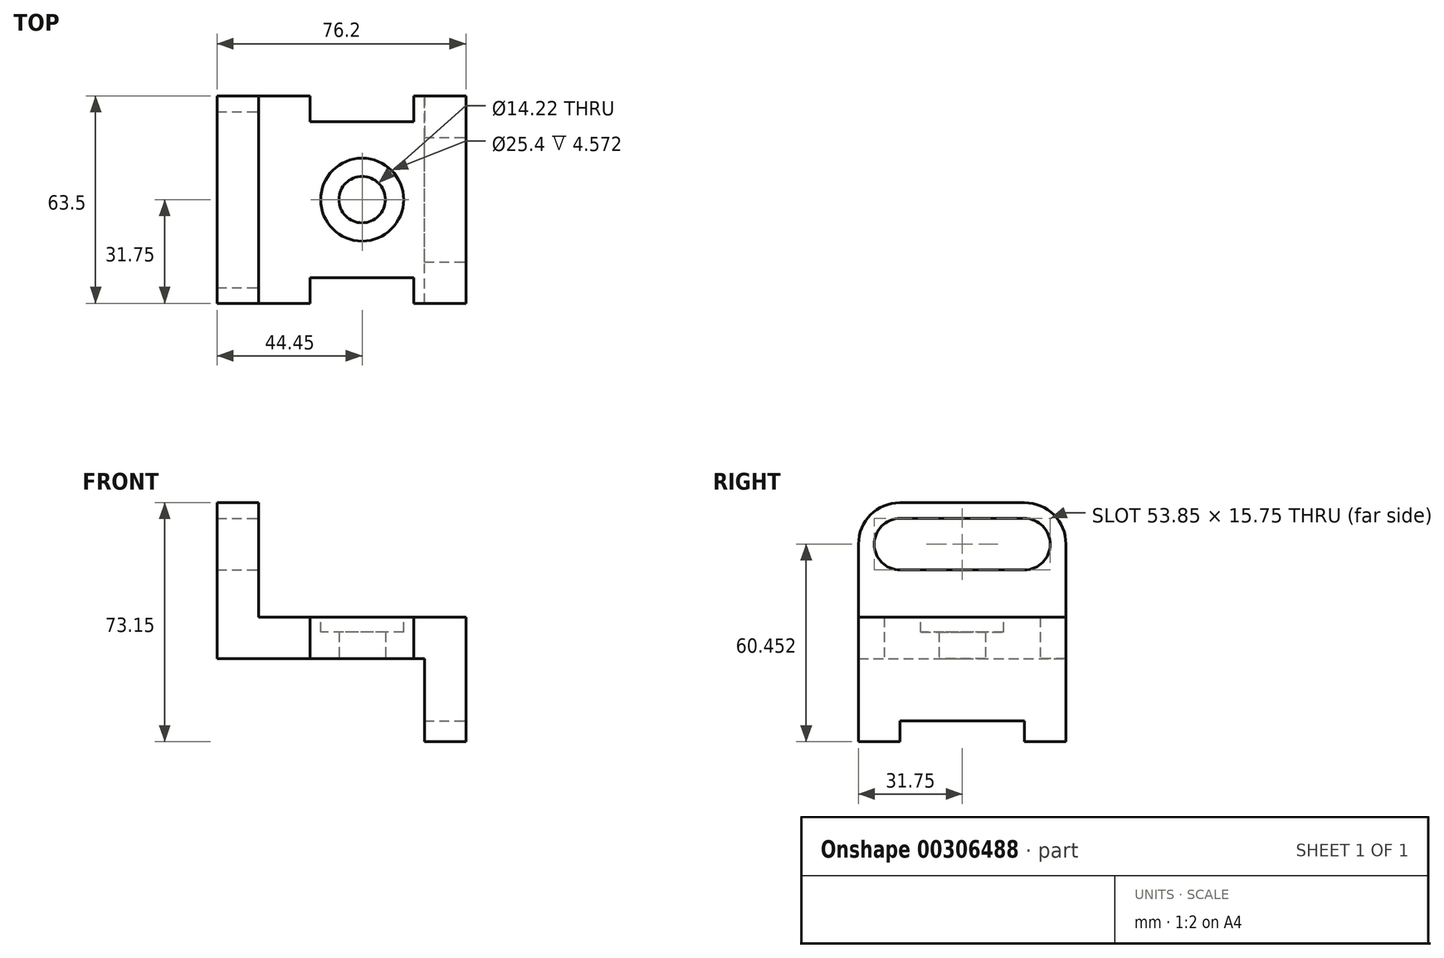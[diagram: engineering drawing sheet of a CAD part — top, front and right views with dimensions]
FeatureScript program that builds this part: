
annotation { "Feature Type Name" : "Feature", "Feature Type Description" : "" }
export const myFeature = defineFeature(function(context is Context, id is Id, definition is map)
    precondition{}
    {
        {
            var Q0;
            Q0=qCreatedBy(makeId("Top.planeOp"),FACE);
            var sketch = newSketch(context, id + "F0", { "sketchPlane" : qUnion([Q0])});
            skLineSegment(sketch, "E0.bottom", {"start": v(0, 0) * mm, "end": v(15.75, 0) * mm});
            skLineSegment(sketch, "E0.top", {"start": v(0, 63.5) * mm, "end": v(15.75, 63.5) * mm});
            skLineSegment(sketch, "E0.left", {"start": v(0, 0) * mm, "end": v(0, 63.5) * mm});
            skLineSegment(sketch, "E0.right", {"start": v(63.5, 0) * mm, "end": v(63.5, 63.5) * mm});
            skLineSegment(sketch, "E1.top", {"start": v(15.75, 7.87) * mm, "end": v(47.5, 7.87) * mm});
            skLineSegment(sketch, "E1.left", {"start": v(15.75, 0) * mm, "end": v(15.75, 7.87) * mm});
            skLineSegment(sketch, "E1.right", {"start": v(47.5, 0) * mm, "end": v(47.5, 7.87) * mm});
            skLineSegment(sketch, "E2.top", {"start": v(15.75, 55.63) * mm, "end": v(47.5, 55.63) * mm});
            skLineSegment(sketch, "E2.left", {"start": v(15.75, 63.5) * mm, "end": v(15.75, 55.63) * mm});
            skLineSegment(sketch, "E2.right", {"start": v(47.5, 63.5) * mm, "end": v(47.5, 55.63) * mm});
            skLineSegment(sketch, "E3.trimOffspring", {"start": v(47.5, 63.5) * mm, "end": v(63.5, 63.5) * mm});
            skLineSegment(sketch, "E4.trimOffspring", {"start": v(47.5, 0) * mm, "end": v(63.5, 0) * mm});
            skCircle(sketch, "E5", {"center": v(31.75, 31.75) * mm, "radius": 7.11 * mm});
            skSolve(sketch);
        }
        {
            var Q0;
            Q0 = qSketchRegion(id + "F0", true);
            extrude(context, id + "F1", {"entities" : qUnion([Q0]), "depth" : 12.7 * mm});
        }
        {
            var Q0;
            Q0=makeQuery(id+"F1.opExtrude","SWEPT_FACE",FACE,{"disambiguationData":[OSD([sQuery(id+"F0.wireOp",EDGE,"E0.right")])]});
            var sketch = newSketch(context, id + "F2", { "sketchPlane" : qUnion([Q0])});
            skLineSegment(sketch, "E6.top", {"start": v(0, -25.4) * mm, "end": v(12.7, -25.4) * mm});
            skLineSegment(sketch, "E6.left", {"start": v(0, -19.05) * mm, "end": v(0, -25.4) * mm});
            skLineSegment(sketch, "E6.right", {"start": v(12.7, -19.05) * mm, "end": v(12.7, -25.4) * mm});
            skLineSegment(sketch, "E7.top", {"start": v(63.5, -25.4) * mm, "end": v(50.8, -25.4) * mm});
            skLineSegment(sketch, "E7.left", {"start": v(63.5, -19.05) * mm, "end": v(63.5, -25.4) * mm});
            skLineSegment(sketch, "E7.right", {"start": v(50.8, -19.05) * mm, "end": v(50.8, -25.4) * mm});
            skLineSegment(sketch, "E8.bottom", {"start": v(12.7, -19.05) * mm, "end": v(50.8, -19.05) * mm});
            skLineSegment(sketch, "E8.top", {"start": v(0, 0) * mm, "end": v(63.5, 0) * mm});
            skLineSegment(sketch, "E8.left", {"start": v(0, -19.05) * mm, "end": v(0, 0) * mm});
            skLineSegment(sketch, "E8.right", {"start": v(63.5, -19.05) * mm, "end": v(63.5, 0) * mm});
            skSolve(sketch);
        }
        {
            var Q0;
            Q0 = qSketchRegion(id + "F2", true);
            extrude(context, id + "F3", {"entities" : qUnion([Q0]), "operationType" : NewBodyOperationType.ADD, "oppositeDirection" : true, "depth" : 12.7 * mm});
        }
        {
            var Q0;
            Q0=makeQuery(id+"F1.opExtrude","CAP_FACE",FACE,{"disambiguationData":[OSD([sQuery(id+"F0.wireOp",EDGE,"E0.bottom"),sQuery(id+"F0.wireOp",EDGE,"E0.top"),sQuery(id+"F0.wireOp",EDGE,"E0.left"),sQuery(id+"F0.wireOp",EDGE,"E0.right"),sQuery(id+"F0.wireOp",EDGE,"E1.top"),sQuery(id+"F0.wireOp",EDGE,"E1.left"),sQuery(id+"F0.wireOp",EDGE,"E1.right"),sQuery(id+"F0.wireOp",EDGE,"E2.top"),sQuery(id+"F0.wireOp",EDGE,"E2.left"),sQuery(id+"F0.wireOp",EDGE,"E2.right"),sQuery(id+"F0.wireOp",EDGE,"E3.trimOffspring"),sQuery(id+"F0.wireOp",EDGE,"E4.trimOffspring"),sQuery(id+"F0.wireOp",EDGE,"E5")])],"isStart":false});
            var sketch = newSketch(context, id + "F4", { "sketchPlane" : qUnion([Q0])});
            skCircle(sketch, "E9", {"center": v(31.75, 31.75) * mm, "radius": 12.7 * mm});
            skSolve(sketch);
        }
        {
            var Q0;
            Q0 = qSketchRegion(id + "F4", true);
            extrude(context, id + "F5", {"entities" : qUnion([Q0]), "operationType" : NewBodyOperationType.REMOVE, "oppositeDirection" : true, "depth" : 4.57 * mm});
        }
        {
            var Q0;
            Q0=makeQuery(id+"F1.opExtrude","SWEPT_FACE",FACE,{"disambiguationData":[OSD([sQuery(id+"F0.wireOp",EDGE,"E0.left")])]});
            var sketch = newSketch(context, id + "F6", { "sketchPlane" : qUnion([Q0])});
            skLineSegment(sketch, "E10.bottom", {"start": v(0, 0) * mm, "end": v(-63.5, 0) * mm});
            skLineSegment(sketch, "E10.top", {"start": v(-12.7, 47.75) * mm, "end": v(-50.8, 47.75) * mm});
            skLineSegment(sketch, "E10.left", {"start": v(0, 0) * mm, "end": v(0, 35.05) * mm});
            skLineSegment(sketch, "E10.right", {"start": v(-63.5, 0) * mm, "end": v(-63.5, 35.05) * mm});
            skPoint(sketch, "E11.visualSharp", {"position": v(-63.5, 47.75) * mm});
            skArc(sketch, "E11.filletArc", {"start": v(-50.8, 47.75) * mm, "mid": v(-59.78, 44.03) * mm, "end": v(-63.5, 35.05) * mm});
            skPoint(sketch, "E12.visualSharp", {"position": v(0, 47.75) * mm});
            skArc(sketch, "E12.filletArc", {"start": v(0, 35.05) * mm, "mid": v(-3.72, 44.03) * mm, "end": v(-12.7, 47.75) * mm});
            skArc(sketch, "E13", {"start": v(-50.8, 42.93) * mm, "mid": v(-58.67, 35.05) * mm, "end": v(-50.8, 27.18) * mm});
            skArc(sketch, "E14", {"start": v(-12.7, 42.93) * mm, "mid": v(-4.83, 35.05) * mm, "end": v(-12.7, 27.18) * mm});
            skLineSegment(sketch, "E15", {"start": v(-50.8, 42.93) * mm, "end": v(-12.7, 42.93) * mm});
            skLineSegment(sketch, "E16", {"start": v(-12.7, 27.18) * mm, "end": v(-50.8, 27.18) * mm});
            skSolve(sketch);
        }
        {
            var Q0;
            Q0 = qSketchRegion(id + "F6", true);
            extrude(context, id + "F7", {"entities" : qUnion([Q0]), "operationType" : NewBodyOperationType.ADD, "depth" : 12.7 * mm});
        }
    });
